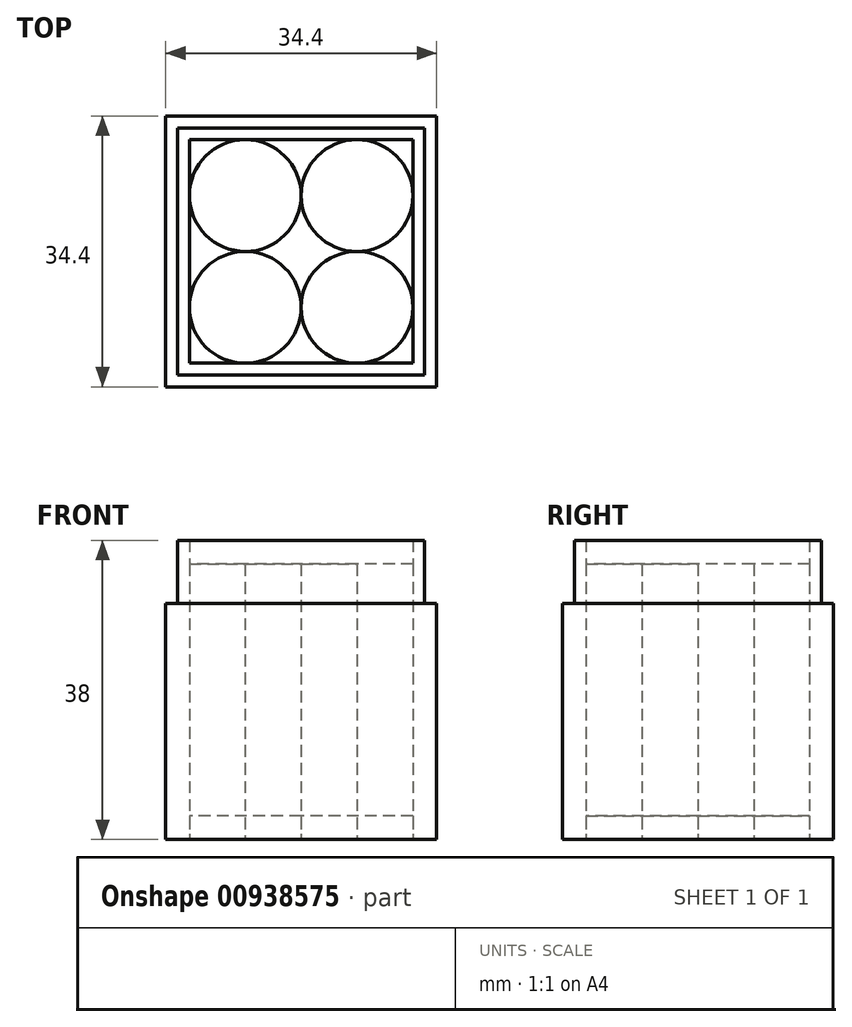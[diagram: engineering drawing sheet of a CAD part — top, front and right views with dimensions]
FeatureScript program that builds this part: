
annotation { "Feature Type Name" : "Feature", "Feature Type Description" : "" }
export const myFeature = defineFeature(function(context is Context, id is Id, definition is map)
    precondition{}
    {
        {
            var Q0;
            Q0=qCreatedBy(makeId("Top.planeOp"),FACE);
            var sketch = newSketch(context, id + "F0", { "sketchPlane" : qUnion([Q0])});
            skLineSegment(sketch, "E0.bottom", {"start": v(17.2, 17.2) * mm, "end": v(-17.2, 17.2) * mm});
            skLineSegment(sketch, "E0.top", {"start": v(17.2, -17.2) * mm, "end": v(-17.2, -17.2) * mm});
            skLineSegment(sketch, "E0.left", {"start": v(17.2, 17.2) * mm, "end": v(17.2, -17.2) * mm});
            skLineSegment(sketch, "E0.right", {"start": v(-17.2, 17.2) * mm, "end": v(-17.2, -17.2) * mm});
            skPoint(sketch, "E0.middle", {"position": v(0, 0) * mm});
            skLineSegment(sketch, "E1.bottom", {"start": v(14.2, 14.2) * mm, "end": v(-14.2, 14.2) * mm});
            skLineSegment(sketch, "E1.top", {"start": v(14.2, -14.2) * mm, "end": v(-14.2, -14.2) * mm});
            skLineSegment(sketch, "E1.left", {"start": v(14.2, 14.2) * mm, "end": v(14.2, -14.2) * mm});
            skLineSegment(sketch, "E1.right", {"start": v(-14.2, 14.2) * mm, "end": v(-14.2, -14.2) * mm});
            skLineSegment(sketch, "E2.bottom", {"start": v(15.7, 15.7) * mm, "end": v(-15.7, 15.7) * mm});
            skLineSegment(sketch, "E2.top", {"start": v(15.7, -15.7) * mm, "end": v(-15.7, -15.7) * mm});
            skLineSegment(sketch, "E2.left", {"start": v(15.7, 15.7) * mm, "end": v(15.7, -15.7) * mm});
            skLineSegment(sketch, "E2.right", {"start": v(-15.7, 15.7) * mm, "end": v(-15.7, -15.7) * mm});
            skLineSegment(sketch, "E3", {"start": v(0, 0) * mm, "end": v(7.1, 0) * mm});
            skLineSegment(sketch, "E4", {"start": v(0, 0) * mm, "end": v(0, 7.1) * mm});
            skLineSegment(sketch, "E5", {"start": v(0, 0) * mm, "end": v(0, -7.1) * mm});
            skLineSegment(sketch, "E6", {"start": v(0, 0) * mm, "end": v(-7.1, 0) * mm});
            skLineSegment(sketch, "E7", {"start": v(-7.1, 0) * mm, "end": v(-7.1, -7.1) * mm});
            skLineSegment(sketch, "E8", {"start": v(-7.1, -7.1) * mm, "end": v(0, -7.1) * mm});
            skLineSegment(sketch, "E9", {"start": v(0, -7.1) * mm, "end": v(7.1, -7.1) * mm});
            skLineSegment(sketch, "E10", {"start": v(7.1, -7.1) * mm, "end": v(7.1, 0) * mm});
            skLineSegment(sketch, "E11", {"start": v(0, 7.1) * mm, "end": v(7.1, 7.1) * mm});
            skPoint(sketch, "E11.endSnap0", {"position": v(7.1, -3.55) * mm});
            skLineSegment(sketch, "E12", {"start": v(7.1, 7.1) * mm, "end": v(7.1, 0) * mm});
            skLineSegment(sketch, "E13", {"start": v(-7.1, 0) * mm, "end": v(-7.1, 7.1) * mm});
            skLineSegment(sketch, "E14", {"start": v(-7.1, 7.1) * mm, "end": v(0, 7.1) * mm});
            skCircle(sketch, "E15", {"center": v(-7.1, 7.1) * mm, "radius": 7.1 * mm});
            skCircle(sketch, "E16", {"center": v(7.1, 7.1) * mm, "radius": 7.1 * mm});
            skCircle(sketch, "E17", {"center": v(7.1, -7.1) * mm, "radius": 7.1 * mm});
            skCircle(sketch, "E18", {"center": v(-7.1, -7.1) * mm, "radius": 7.1 * mm});
            skSolve(sketch);
        }
        {
            var Q0;
            Q0=makeQuery(id+"F0.imprint","IMPRINT",FACE,{"disambiguationData":[TD([[makeQuery(id+"F0.imprint","IMPRINT",EDGE,{"derivedFrom":sQuery(id+"F0.wireOp",EDGE,"E2.bottom")}),1.0]])]});
            extrude(context, id + "F1", {"entities" : qUnion([Q0]), "depth" : 38 * mm, "offsetDistance" : 25.4 * mm});
        }
        {
            var Q0;
            Q0 = qSketchRegion(id + "F0", true);
            var Q1;
            Q1 = qConstructionFilter(qBodyType(qCreatedBy(id + "F0" ,EDGE), BodyType.WIRE), ConstructionObject.NO);
            extrude(context, id + "F2", {"entities" : qUnion([Q0]), "operationType" : NewBodyOperationType.ADD, "surfaceEntities" : qUnion([Q1]), "depth" : 30 * mm, "offsetDistance" : 25.4 * mm});
        }
        {
            var Q0;
            {var subQ0=sQuery(id+"F0.wireOp",EDGE,"E1.right");var subQ1=sQuery(id+"F0.wireOp",EDGE,"E1.bottom");var subQ2=makeQuery(id+"F0.imprint","INTERSECT",VERTEX,{"derivedFrom":[subQ1,subQ0]});Q0=makeQuery(id+"F0.imprint","IMPRINT",FACE,{"disambiguationData":[TD([[makeQuery(id+"F0.imprint","IMPRINT",EDGE,{"disambiguationData":[TD([[subQ2,1.0]])],"derivedFrom":subQ1}),1.0]])]});}
            var Q1;
            {var subQ0=sQuery(id+"F0.wireOp",EDGE,"E16");var subQ1=sQuery(id+"F0.wireOp",EDGE,"E1.bottom");var subQ2=makeQuery(id+"F0.imprint","INTERSECT",VERTEX,{"derivedFrom":[subQ1,subQ0]});Q1=makeQuery(id+"F0.imprint","IMPRINT",FACE,{"disambiguationData":[TD([[makeQuery(id+"F0.imprint","IMPRINT",EDGE,{"disambiguationData":[TD([[subQ2,-1.0]])],"derivedFrom":subQ1}),1.0]])]});}
            var Q2;
            {var subQ0=sQuery(id+"F0.wireOp",EDGE,"E1.left");var subQ1=sQuery(id+"F0.wireOp",EDGE,"E1.bottom");var subQ2=makeQuery(id+"F0.imprint","INTERSECT",VERTEX,{"derivedFrom":[subQ1,subQ0]});Q2=makeQuery(id+"F0.imprint","IMPRINT",FACE,{"disambiguationData":[TD([[makeQuery(id+"F0.imprint","IMPRINT",EDGE,{"disambiguationData":[TD([[subQ2,-1.0]])],"derivedFrom":subQ1}),1.0]])]});}
            var Q3;
            {var subQ0=sQuery(id+"F0.wireOp",EDGE,"E16");var subQ1=sQuery(id+"F0.wireOp",EDGE,"E1.left");var subQ2=makeQuery(id+"F0.imprint","INTERSECT",VERTEX,{"derivedFrom":[subQ1,subQ0]});Q3=makeQuery(id+"F0.imprint","IMPRINT",FACE,{"disambiguationData":[TD([[makeQuery(id+"F0.imprint","IMPRINT",EDGE,{"disambiguationData":[TD([[subQ2,-1.0]])],"derivedFrom":subQ1}),-1.0]])]});}
            var Q4;
            {var subQ0=sQuery(id+"F0.wireOp",EDGE,"E3");Q4=makeQuery(id+"F0.imprint","IMPRINT",FACE,{"disambiguationData":[TD([[makeQuery(id+"F0.imprint","IMPRINT",EDGE,{"derivedFrom":subQ0}),1.0]])]});}
            var Q5;
            {var subQ0=sQuery(id+"F0.wireOp",EDGE,"E4");Q5=makeQuery(id+"F0.imprint","IMPRINT",FACE,{"disambiguationData":[TD([[makeQuery(id+"F0.imprint","IMPRINT",EDGE,{"derivedFrom":subQ0}),1.0]])]});}
            var Q6;
            {var subQ0=sQuery(id+"F0.wireOp",EDGE,"E5");Q6=makeQuery(id+"F0.imprint","IMPRINT",FACE,{"disambiguationData":[TD([[makeQuery(id+"F0.imprint","IMPRINT",EDGE,{"derivedFrom":subQ0}),-1.0]])]});}
            var Q7;
            {var subQ0=sQuery(id+"F0.wireOp",EDGE,"E3");Q7=makeQuery(id+"F0.imprint","IMPRINT",FACE,{"disambiguationData":[TD([[makeQuery(id+"F0.imprint","IMPRINT",EDGE,{"derivedFrom":subQ0}),-1.0]])]});}
            var Q8;
            {var subQ0=sQuery(id+"F0.wireOp",EDGE,"E15");var subQ1=sQuery(id+"F0.wireOp",EDGE,"E1.right");var subQ2=makeQuery(id+"F0.imprint","INTERSECT",VERTEX,{"derivedFrom":[subQ1,subQ0]});Q8=makeQuery(id+"F0.imprint","IMPRINT",FACE,{"disambiguationData":[TD([[makeQuery(id+"F0.imprint","IMPRINT",EDGE,{"disambiguationData":[TD([[subQ2,-1.0]])],"derivedFrom":subQ1}),1.0]])]});}
            var Q9;
            {var subQ0=sQuery(id+"F0.wireOp",EDGE,"E1.right");var subQ1=sQuery(id+"F0.wireOp",EDGE,"E1.top");var subQ2=makeQuery(id+"F0.imprint","INTERSECT",VERTEX,{"derivedFrom":[subQ1,subQ0]});Q9=makeQuery(id+"F0.imprint","IMPRINT",FACE,{"disambiguationData":[TD([[makeQuery(id+"F0.imprint","IMPRINT",EDGE,{"disambiguationData":[TD([[subQ2,1.0]])],"derivedFrom":subQ1}),-1.0]])]});}
            var Q10;
            {var subQ0=sQuery(id+"F0.wireOp",EDGE,"E17");var subQ1=sQuery(id+"F0.wireOp",EDGE,"E1.top");var subQ2=makeQuery(id+"F0.imprint","INTERSECT",VERTEX,{"derivedFrom":[subQ1,subQ0]});Q10=makeQuery(id+"F0.imprint","IMPRINT",FACE,{"disambiguationData":[TD([[makeQuery(id+"F0.imprint","IMPRINT",EDGE,{"disambiguationData":[TD([[subQ2,-1.0]])],"derivedFrom":subQ1}),-1.0]])]});}
            var Q11;
            {var subQ0=sQuery(id+"F0.wireOp",EDGE,"E1.left");var subQ1=sQuery(id+"F0.wireOp",EDGE,"E1.top");var subQ2=makeQuery(id+"F0.imprint","INTERSECT",VERTEX,{"derivedFrom":[subQ1,subQ0]});Q11=makeQuery(id+"F0.imprint","IMPRINT",FACE,{"disambiguationData":[TD([[makeQuery(id+"F0.imprint","IMPRINT",EDGE,{"disambiguationData":[TD([[subQ2,-1.0]])],"derivedFrom":subQ1}),-1.0]])]});}
            extrude(context, id + "F3", {"entities" : qUnion([Q0, Q1, Q2, Q3, Q4, Q5, Q6, Q7, Q8, Q9, Q10, Q11]), "operationType" : NewBodyOperationType.ADD, "depth" : 35 * mm, "offsetDistance" : 25.4 * mm});
        }
        {
            var Q0;
            {var subQ3=sQuery(id+"F0.wireOp",EDGE,"E7");Q0=makeQuery(id+"F0.imprint","IMPRINT",FACE,{"disambiguationData":[TD([[makeQuery(id+"F0.imprint","IMPRINT",EDGE,{"derivedFrom":subQ3}),-1.0]])]});}
            var Q1;
            {var subQ4=sQuery(id+"F0.wireOp",EDGE,"E13");Q1=makeQuery(id+"F0.imprint","IMPRINT",FACE,{"disambiguationData":[TD([[makeQuery(id+"F0.imprint","IMPRINT",EDGE,{"derivedFrom":subQ4}),1.0]])]});}
            var Q2;
            {var subQ0=sQuery(id+"F0.wireOp",EDGE,"E7");Q2=makeQuery(id+"F0.imprint","IMPRINT",FACE,{"disambiguationData":[TD([[makeQuery(id+"F0.imprint","IMPRINT",EDGE,{"derivedFrom":subQ0}),1.0]])]});}
            var Q3;
            {var subQ0=sQuery(id+"F0.wireOp",EDGE,"E13");Q3=makeQuery(id+"F0.imprint","IMPRINT",FACE,{"disambiguationData":[TD([[makeQuery(id+"F0.imprint","IMPRINT",EDGE,{"derivedFrom":subQ0}),-1.0]])]});}
            var Q4;
            {var subQ3=sQuery(id+"F0.wireOp",EDGE,"E9");Q4=makeQuery(id+"F0.imprint","IMPRINT",FACE,{"disambiguationData":[TD([[makeQuery(id+"F0.imprint","IMPRINT",EDGE,{"derivedFrom":subQ3}),-1.0]])]});}
            var Q5;
            {var subQ0=sQuery(id+"F0.wireOp",EDGE,"E9");Q5=makeQuery(id+"F0.imprint","IMPRINT",FACE,{"disambiguationData":[TD([[makeQuery(id+"F0.imprint","IMPRINT",EDGE,{"derivedFrom":subQ0}),1.0]])]});}
            var Q6;
            {var subQ1=sQuery(id+"F0.wireOp",EDGE,"E11");Q6=makeQuery(id+"F0.imprint","IMPRINT",FACE,{"disambiguationData":[TD([[makeQuery(id+"F0.imprint","IMPRINT",EDGE,{"derivedFrom":subQ1}),1.0]])]});}
            var Q7;
            {var subQ0=sQuery(id+"F0.wireOp",EDGE,"E11");Q7=makeQuery(id+"F0.imprint","IMPRINT",FACE,{"disambiguationData":[TD([[makeQuery(id+"F0.imprint","IMPRINT",EDGE,{"derivedFrom":subQ0}),-1.0]])]});}
            extrude(context, id + "F4", {"entities" : qUnion([Q0, Q1, Q2, Q3, Q4, Q5, Q6, Q7]), "depth" : 3 * mm, "offsetDistance" : 25.4 * mm});
        }
    });
